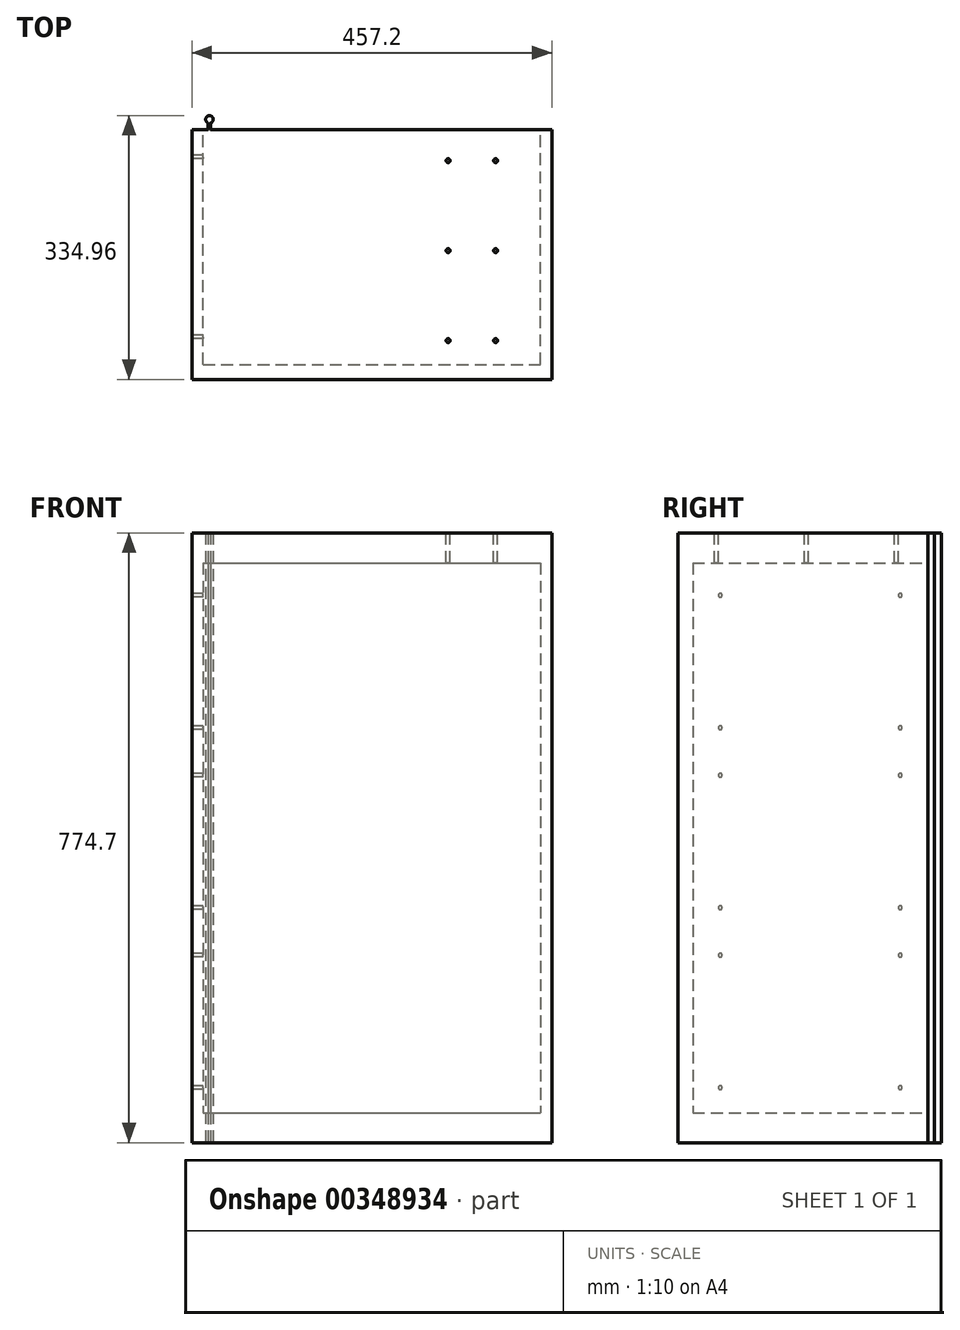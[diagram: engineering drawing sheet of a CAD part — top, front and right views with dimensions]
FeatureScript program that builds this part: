
annotation { "Feature Type Name" : "Feature", "Feature Type Description" : "" }
export const myFeature = defineFeature(function(context is Context, id is Id, definition is map)
    precondition{}
    {
        {
            var Q0;
            Q0=qCreatedBy(makeId("Front.planeOp"),FACE);
            var sketch = newSketch(context, id + "F0", { "sketchPlane" : qUnion([Q0])});
            skLineSegment(sketch, "E0.bottom", {"start": v(228.6, 0) * mm, "end": v(-228.6, 0) * mm});
            skLineSegment(sketch, "E0.top", {"start": v(228.6, 774.7) * mm, "end": v(-228.6, 774.7) * mm});
            skLineSegment(sketch, "E0.left", {"start": v(228.6, 0) * mm, "end": v(228.6, 774.7) * mm});
            skLineSegment(sketch, "E0.right", {"start": v(-228.6, 0) * mm, "end": v(-228.6, 774.7) * mm});
            skPoint(sketch, "E0.middle", {"position": v(0, 387.35) * mm});
            skSolve(sketch);
        }
        {
            var Q0;
            Q0 = qSketchRegion(id + "F0", true);
            extrude(context, id + "F1", {"entities" : qUnion([Q0]), "depth" : 317.5 * mm});
        }
        {
            var Q0;
            Q0=qCreatedBy(makeId("Front.planeOp"),FACE);
            var sketch = newSketch(context, id + "F2", { "sketchPlane" : qUnion([Q0])});
            skLineSegment(sketch, "E1.bottom", {"start": v(-190.5, 38.1) * mm, "end": v(190.5, 38.1) * mm});
            skLineSegment(sketch, "E1.top", {"start": v(-190.5, 736.6) * mm, "end": v(190.5, 736.6) * mm});
            skLineSegment(sketch, "E1.left", {"start": v(-190.5, 38.1) * mm, "end": v(-190.5, 736.6) * mm});
            skLineSegment(sketch, "E1.right", {"start": v(190.5, 38.1) * mm, "end": v(190.5, 736.6) * mm});
            skPoint(sketch, "E1.middle", {"position": v(0, 387.35) * mm});
            skSolve(sketch);
        }
        {
            var Q0;
            Q0=qCreatedBy(makeId("Front.planeOp"),FACE);
            var sketch = newSketch(context, id + "F3", { "sketchPlane" : qUnion([Q0])});
            skLineSegment(sketch, "E2.bottom", {"start": v(-214.31, 736.6) * mm, "end": v(214.31, 736.6) * mm});
            skLineSegment(sketch, "E2.top", {"start": v(-214.31, 38.1) * mm, "end": v(214.31, 38.1) * mm});
            skLineSegment(sketch, "E2.left", {"start": v(-214.31, 736.6) * mm, "end": v(-214.31, 38.1) * mm});
            skLineSegment(sketch, "E2.right", {"start": v(214.31, 736.6) * mm, "end": v(214.31, 38.1) * mm});
            skPoint(sketch, "E2.middle", {"position": v(0, 387.35) * mm});
            skSolve(sketch);
        }
        {
            var Q0;
            Q0 = qSketchRegion(id + "F2", true);
            var Q1;
            Q1 = qSketchRegion(id + "F3", true);
            extrude(context, id + "F4", {"entities" : qUnion([Q0, Q1]), "operationType" : NewBodyOperationType.REMOVE, "depth" : 298.45 * mm, "offsetDistance" : 25.4 * mm});
        }
        {
            var Q0;
            Q0 = qSketchRegion(id + "F3", true);
            extrude(context, id + "F5", {"entities" : qUnion([Q0]), "operationType" : NewBodyOperationType.REMOVE, "depth" : 298.45 * mm, "hasSecondDirection" : true, "secondDirectionOppositeDirection" : false, "secondDirectionDepth" : 19.05 * mm});
        }
        {
            var Q0;
            Q0=qCreatedBy(makeId("Top.planeOp"),FACE);
            var sketch = newSketch(context, id + "F6", { "sketchPlane" : qUnion([Q0])});
            skArc(sketch, "E3", {"start": v(-204.79, 8.2) * mm, "mid": v(-206.38, 17.46) * mm, "end": v(-207.96, 8.2) * mm});
            skLineSegment(sketch, "E4", {"start": v(-204.79, 8.2) * mm, "end": v(-204.79, 0) * mm});
            skLineSegment(sketch, "E5", {"start": v(-207.96, 8.2) * mm, "end": v(-207.96, 0) * mm});
            skLineSegment(sketch, "E6", {"start": v(-207.96, 0) * mm, "end": v(-204.79, 0) * mm});
            skLineSegment(sketch, "E7", {"start": v(-206.38, 12.7) * mm, "end": v(-206.38, 0) * mm, "construction": true});
            skSolve(sketch);
        }
        {
            var Q0;
            Q0=makeQuery(id+"F6.imprint","IMPRINT",FACE,{"disambiguationData":[TD([[makeQuery(id+"F6.imprint","IMPRINT",EDGE,{"derivedFrom":sQuery(id+"F6.wireOp",EDGE,"E3")}),1.0]])]});
            var Q1;
            Q1=makeQuery(id+"F1.opExtrude","SWEPT_FACE",FACE,{"disambiguationData":[OSD([sQuery(id+"F0.wireOp",EDGE,"E0.top")])]});
            extrude(context, id + "F7", {"entities" : qUnion([Q0]), "operationType" : NewBodyOperationType.ADD, "endBound" : BoundingType.UP_TO_SURFACE, "endBoundEntityFace" : qUnion([Q1]), "depth" : 768.35 * mm});
        }
        {
            var Q0;
            {var subQ0=sQuery(id+"F0.wireOp",EDGE,"E0.top");Q0=makeQuery(id+"F7.boolean.opBoolean","MERGE",FACE,{"derivedFrom":[makeQuery(id+"F1.opExtrude","SWEPT_FACE",FACE,{"disambiguationData":[OSD([subQ0])]}),makeQuery(id+"F7.opExtrude","CAP_FACE",FACE,{"disambiguationData":[OSD([subQ0])],"isStart":false})]});}
            var sketch = newSketch(context, id + "F8", { "sketchPlane" : qUnion([Q0])});
            skLineSegment(sketch, "E8", {"start": v(96.84, -39.69) * mm, "end": v(157.16, -39.69) * mm, "construction": true});
            skLineSegment(sketch, "E9", {"start": v(96.84, -153.99) * mm, "end": v(96.84, -268.29) * mm, "construction": true});
            skLineSegment(sketch, "E10", {"start": v(157.16, -268.29) * mm, "end": v(157.16, -153.99) * mm, "construction": true});
            skLineSegment(sketch, "E11", {"start": v(157.16, -39.69) * mm, "end": v(157.16, -153.99) * mm, "construction": true});
            skLineSegment(sketch, "E12", {"start": v(96.84, -153.99) * mm, "end": v(96.84, -39.69) * mm, "construction": true});
            skPoint(sketch, "E13", {"position": v(96.84, -268.29) * mm});
            skPoint(sketch, "E14", {"position": v(96.84, -153.99) * mm});
            skPoint(sketch, "E15", {"position": v(96.84, -39.69) * mm});
            skPoint(sketch, "E16", {"position": v(157.16, -153.99) * mm});
            skPoint(sketch, "E17", {"position": v(157.16, -39.69) * mm});
            skPoint(sketch, "E18", {"position": v(157.16, -268.29) * mm});
            skSolve(sketch);
        }
        {
            var Q0;
            Q0=sQuery(id+"F8.wireOp",VERTEX,"4f9a2164-60a7-4399-89db-87dc29b434f5");
            var Q1;
            Q1=sQuery(id+"F8.wireOp",VERTEX,"7cabd27e-4b16-4863-9737-0d3b4870960d");
            var Q2;
            Q2=sQuery(id+"F8.wireOp",VERTEX,"4dae91c8-48e5-4662-89d8-aaca0527ace0");
            var Q3;
            Q3=sQuery(id+"F8.wireOp",VERTEX,"35c6a2ad-284f-49ac-947f-ae7e166f7cbb");
            var Q4;
            Q4=sQuery(id+"F8.wireOp",VERTEX,"aa288cf3-4cfa-41a3-86be-cae0eb7e31a3");
            var Q5;
            Q5=sQuery(id+"F8.wireOp",VERTEX,"E14");
            var Q6;
            Q6=sQuery(id+"F8.wireOp",VERTEX,"275c8b97-2b5a-4726-a6d2-827bb33cb39e");
            var Q7;
            Q7=sQuery(id+"F8.wireOp",VERTEX,"E17");
            var Q8;
            Q8=sQuery(id+"F8.wireOp",VERTEX,"7af0d288-0d83-4324-b4dd-7fab062837cc");
            var Q9;
            Q9=sQuery(id+"F8.wireOp",VERTEX,"ba236326-ac3f-4813-bb2d-2a1361a1a503");
            var Q10;
            Q10=sQuery(id+"F8.wireOp",VERTEX,"E16");
            var Q11;
            Q11=sQuery(id+"F8.wireOp",VERTEX,"70eb8efb-2a7e-4254-9342-28a2bc500242");
            var Q12;
            Q12=sQuery(id+"F8.wireOp",VERTEX,"93b7b2f8-2d8c-4ec6-ab9a-8d7a589dbbed");
            var Q13;
            Q13=sQuery(id+"F8.wireOp",VERTEX,"bc3557d1-57eb-49d3-99af-c708edc07982");
            var Q14;
            Q14=sQuery(id+"F8.wireOp",VERTEX,"E13");
            var Q15;
            Q15=sQuery(id+"F8.wireOp",VERTEX,"a18b8d8b-0e3b-4850-b0ec-280f819ac566");
            var Q16;
            Q16=sQuery(id+"F8.wireOp",VERTEX,"72903474-dbae-47b1-a57f-400124e25195");
            var Q17;
            Q17=sQuery(id+"F8.wireOp",VERTEX,"f8143e2b-1727-4708-a22c-3508af5bd33a");
            var Q18;
            Q18=sQuery(id+"F8.wireOp",VERTEX,"0a1c0e9a-90a4-4e19-8414-528367622541");
            var Q19;
            Q19=sQuery(id+"F8.wireOp",VERTEX,"87e5ee0e-8e72-4712-a111-953b97608e2c");
            var Q20;
            Q20=sQuery(id+"F8.wireOp",VERTEX,"9065aa7a-8f52-47da-ae97-7fb593a7d007");
            var Q21;
            Q21=sQuery(id+"F8.wireOp",VERTEX,"E15");
            var Q22;
            Q22=sQuery(id+"F8.wireOp",VERTEX,"E18");
            var Q23;
            Q23=sQuery(id+"F8.wireOp",VERTEX,"42a323e7-b877-4ab8-a31c-86bcfbef5f85");
            var Q24;
            Q24=makeQuery(id+"F1.opExtrude","SWEPT_BODY",BODY,{"disambiguationData":[OSD([sQuery(id+"F0.wireOp",EDGE,"E0.bottom"),sQuery(id+"F0.wireOp",EDGE,"E0.top"),sQuery(id+"F0.wireOp",EDGE,"E0.left"),sQuery(id+"F0.wireOp",EDGE,"E0.right")])]});
            hole(context, id + "F9", {"style" : HoleStyle.SIMPLE, "endStyle" : HoleEndStyle.BLIND, "standardTappedOrClearance" : lookupTablePath({ "standard" : "ANSI", "size" : "#10 (0.2)", "type" : "Drilled" }), "standardBlindInLast" : lookupTablePath({ "standard" : "ANSI", "size" : "#10", "type" : "Drilled" }), "holeDiameter" : 4.9 * mm, "holeDepth" : 38.1 * mm, "isTappedThrough" : true, "tappedDepth" : 12.7 * mm, "tapClearance" : 3, "locations" : qUnion([Q0, Q1, Q2, Q3, Q4, Q5, Q6, Q7, Q8, Q9, Q10, Q11, Q12, Q13, Q14, Q15, Q16, Q17, Q18, Q19, Q20, Q21, Q22, Q23]), "scope" : qUnion([Q24])});
        }
        {
            var Q0;
            Q0=makeQuery(id+"F1.opExtrude","SWEPT_FACE",FACE,{"disambiguationData":[OSD([sQuery(id+"F0.wireOp",EDGE,"E0.right")])]});
            var sketch = newSketch(context, id + "F10", { "sketchPlane" : qUnion([Q0])});
            skLineSegment(sketch, "E19", {"start": v(149.23, 69.85) * mm, "end": v(149.22, 238.12) * mm, "construction": true});
            skLineSegment(sketch, "E20", {"start": v(149.22, 238.12) * mm, "end": v(149.22, 298.45) * mm, "construction": true});
            skLineSegment(sketch, "E21", {"start": v(149.22, 298.45) * mm, "end": v(149.22, 466.72) * mm, "construction": true});
            skLineSegment(sketch, "E22", {"start": v(149.22, 466.72) * mm, "end": v(149.22, 527.05) * mm, "construction": true});
            skLineSegment(sketch, "E23", {"start": v(149.22, 527.05) * mm, "end": v(149.22, 695.32) * mm, "construction": true});
            skLineSegment(sketch, "E24", {"start": v(149.23, 69.85) * mm, "end": v(263.53, 69.85) * mm, "construction": true});
            skLineSegment(sketch, "E25", {"start": v(34.93, 69.85) * mm, "end": v(149.23, 69.85) * mm, "construction": true});
            skLineSegment(sketch, "E26", {"start": v(149.22, 238.12) * mm, "end": v(263.53, 238.12) * mm, "construction": true});
            skLineSegment(sketch, "E27", {"start": v(149.22, 298.45) * mm, "end": v(263.53, 298.45) * mm, "construction": true});
            skLineSegment(sketch, "E28", {"start": v(149.22, 466.72) * mm, "end": v(263.53, 466.72) * mm, "construction": true});
            skLineSegment(sketch, "E29", {"start": v(149.22, 527.05) * mm, "end": v(263.53, 527.05) * mm, "construction": true});
            skLineSegment(sketch, "E30", {"start": v(149.22, 695.32) * mm, "end": v(263.53, 695.32) * mm, "construction": true});
            skLineSegment(sketch, "E31", {"start": v(34.93, 238.12) * mm, "end": v(149.22, 238.12) * mm, "construction": true});
            skLineSegment(sketch, "E32", {"start": v(34.92, 298.45) * mm, "end": v(149.22, 298.45) * mm, "construction": true});
            skLineSegment(sketch, "E33", {"start": v(34.93, 466.72) * mm, "end": v(149.22, 466.72) * mm, "construction": true});
            skLineSegment(sketch, "E34", {"start": v(34.92, 527.05) * mm, "end": v(149.22, 527.05) * mm, "construction": true});
            skLineSegment(sketch, "E35", {"start": v(34.93, 695.32) * mm, "end": v(149.22, 695.32) * mm, "construction": true});
            skCircle(sketch, "E36", {"center": v(34.93, 695.32) * mm, "radius": 2.41 * mm});
            skCircle(sketch, "E37", {"center": v(34.92, 527.05) * mm, "radius": 2.41 * mm});
            skCircle(sketch, "E38", {"center": v(34.93, 466.72) * mm, "radius": 2.41 * mm});
            skCircle(sketch, "E39", {"center": v(34.92, 298.45) * mm, "radius": 2.41 * mm});
            skCircle(sketch, "E40", {"center": v(34.93, 238.12) * mm, "radius": 2.41 * mm});
            skCircle(sketch, "E41", {"center": v(34.93, 69.85) * mm, "radius": 2.41 * mm});
            skCircle(sketch, "E42", {"center": v(263.53, 69.85) * mm, "radius": 2.41 * mm});
            skCircle(sketch, "E43", {"center": v(263.53, 238.12) * mm, "radius": 2.41 * mm});
            skCircle(sketch, "E44", {"center": v(263.53, 298.45) * mm, "radius": 2.41 * mm});
            skCircle(sketch, "E45", {"center": v(263.53, 466.72) * mm, "radius": 2.41 * mm});
            skCircle(sketch, "E46", {"center": v(263.53, 527.05) * mm, "radius": 2.41 * mm});
            skCircle(sketch, "E47", {"center": v(263.53, 695.32) * mm, "radius": 2.41 * mm});
            skSolve(sketch);
        }
        {
            var Q0;
            Q0 = qSketchRegion(id + "F10", true);
            extrude(context, id + "F11", {"entities" : qUnion([Q0]), "operationType" : NewBodyOperationType.REMOVE, "oppositeDirection" : true, "depth" : 25.4 * mm});
        }
    });
